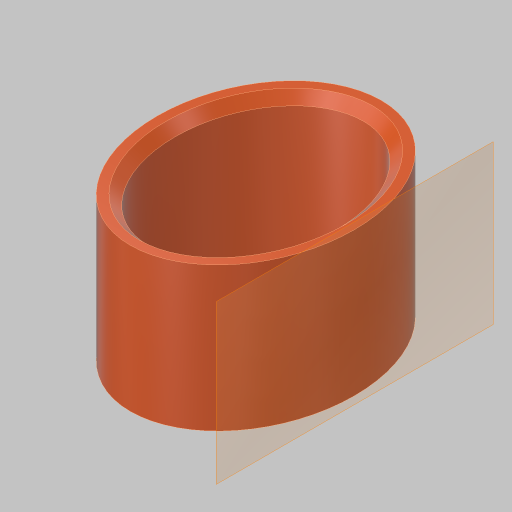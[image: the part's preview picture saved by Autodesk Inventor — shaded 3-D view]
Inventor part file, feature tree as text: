
AUTODESK INVENTOR PART (.ipt)
format: ipt  version: 2023.5 (Build 275446000, 446)  size: 160,768 bytes
history: native  units: in
note: dims shown in document units (in); Inventor stores cm internally (conversion verified against a paired STEP export)
features: extrude x2, sketch x2, chamfer x1, plane x1, projected_geometry x1
ambient origin geometry x8: Origin, YZ Plane, XZ Plane, XY Plane, X Axis, Y Axis, Z Axis, Center Point
bodies: Solid1 (feature_tree)
feature tree (7):
  extrude  "Extrusion1"  Depth=0.8725in
  chamfer  "Chamfer1"  Distance=1.0in
  plane  "Work Plane1"
  extrude  "Extrusion2"  Depth=0.0625in TaperAngle=45.0deg
  sketch  "Sketch1"  dims[d0=0.685in d1=0.8725in]
  sketch  "Sketch2"  dims[d2=0.125in d3=1.0in d4=0.0in d5=0.0625in d6=0.125in d7=45.0deg d8=0.688in d9=1.25in d10=0.5in d11=0.2638in d12=1.0in d13=0.0in]
  projected_geometry  "Projected Loop1"
